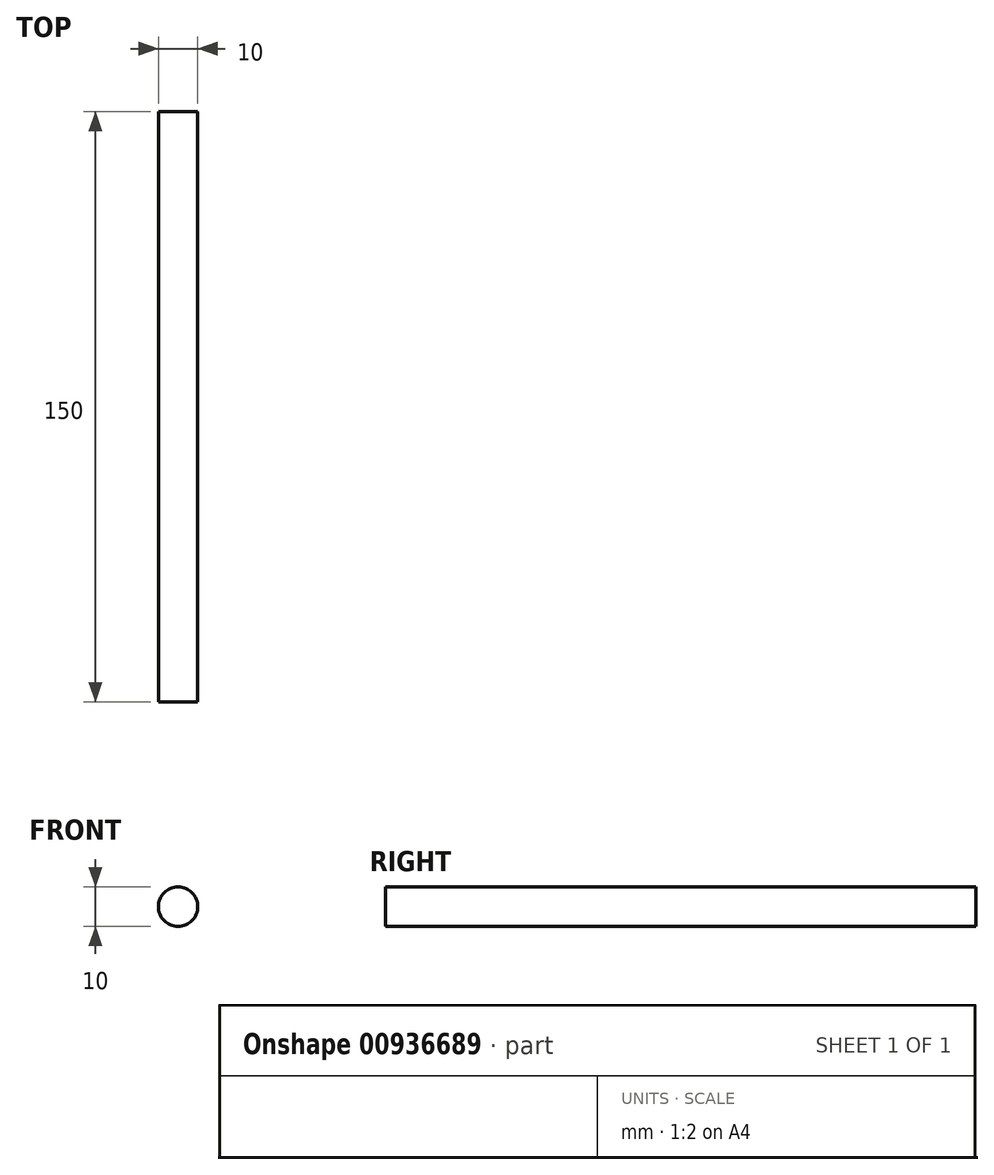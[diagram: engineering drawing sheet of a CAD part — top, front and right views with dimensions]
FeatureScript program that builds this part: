
annotation { "Feature Type Name" : "Feature", "Feature Type Description" : "" }
export const myFeature = defineFeature(function(context is Context, id is Id, definition is map)
    precondition{}
    {
        {
            var Q0;
            Q0=qCreatedBy(makeId("Front.planeOp"),FACE);
            var sketch = newSketch(context, id + "F0", { "sketchPlane" : qUnion([Q0])});
            skCircle(sketch, "E0", {"center": v(0, 0) * mm, "radius": 5 * mm});
            skSolve(sketch);
        }
        {
            var Q0;
            Q0=makeQuery(id+"F0.imprint","IMPRINT",FACE,{"disambiguationData":[TD([[makeQuery(id+"F0.imprint","IMPRINT",EDGE,{"derivedFrom":sQuery(id+"F0.wireOp",EDGE,"E0")}),1.0]])]});
            extrude(context, id + "F1", {"entities" : qUnion([Q0]), "depth" : 150 * mm, "offsetDistance" : 25 * mm});
        }
    });
